# Revit family: Haworth_Downtown_Chair_Executive
name_source: partatom
category: Furniture
revit_build: Autodesk Revit 2018 (Build: 20170223_1515(x64)
units: mm (PartAtom-declared; Revit-internal decimal feet)

## family parameters
Always vertical = Yes
Cut with Voids When Loaded = No
OmniClass Number = 23.40.20.00
OmniClass Title = General Furniture and Specialties
Room Calculation Point = No
Shared = No
Work Plane-Based = No

## types (1)
- HCPF-DE5L - Executive
    Actual Depth = 2' - 2 1/2"
    Actual Height = 3' - 5 3/4"
    Actual Width = 2' - 3 1/4"
    Assembly Code = E2020200
    Description = Haworth Downtown Chair - Executive
    Manufacturer = Haworth
    Model = HCPF-DE5L
    Size = Verify Final Dim. w/ Haworth
    Trim Finish = Haworth _ Polymer _ Black
    URL = http://www.haworth.com
    URL - Product = http://www.haworth.com
    Version = 3
    Warranty = http://www.haworth.com

## geometry (parser evidence)
native form markers: Blend x8, Sweep x3
no freeform markers — native parametric forms only
